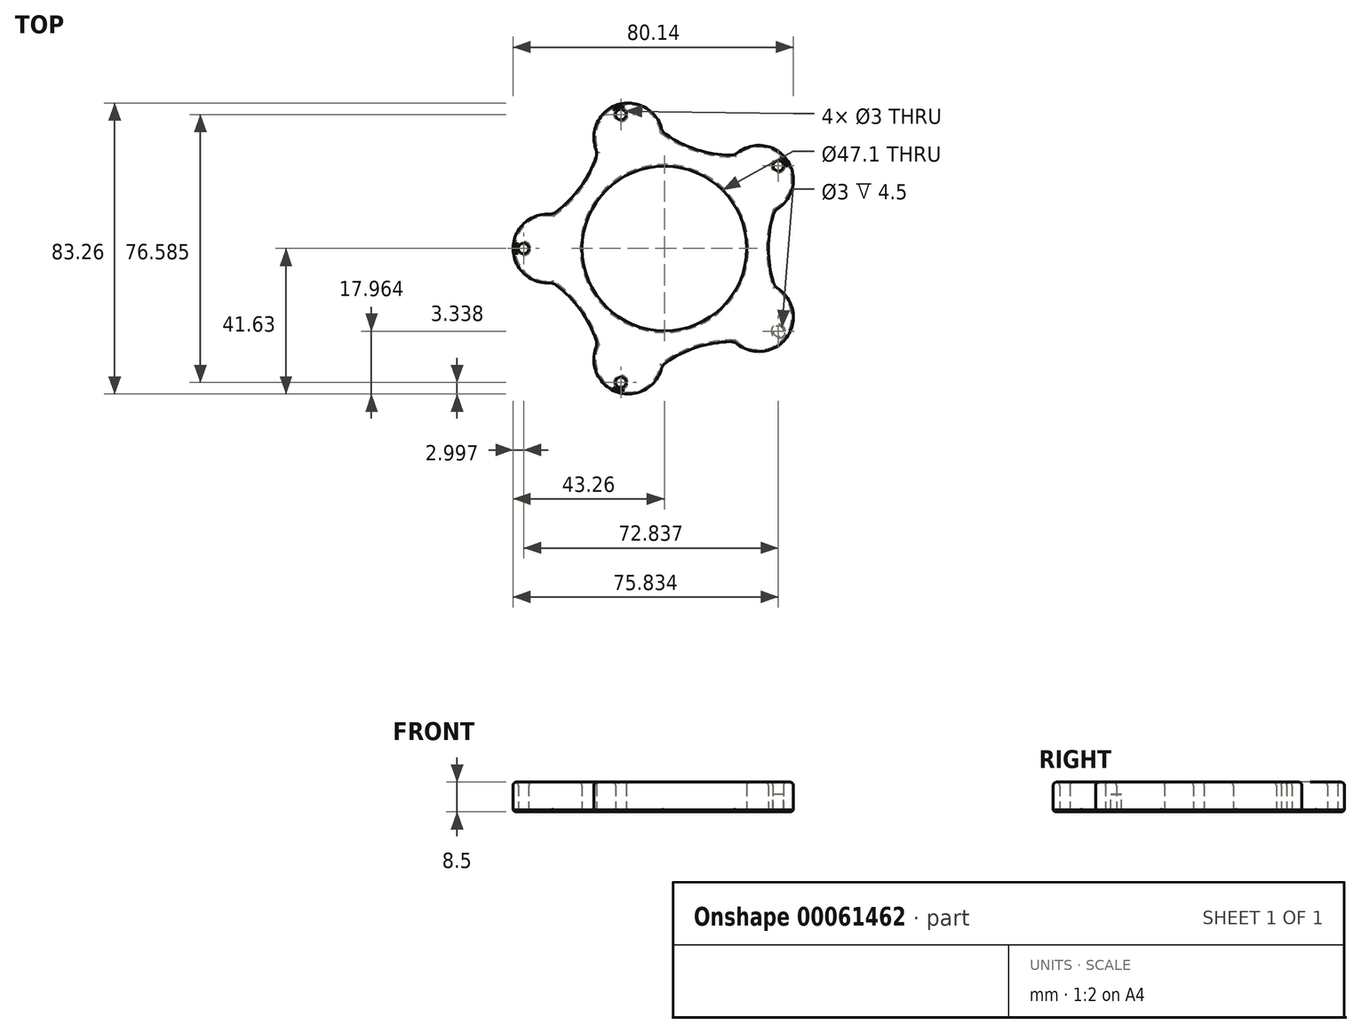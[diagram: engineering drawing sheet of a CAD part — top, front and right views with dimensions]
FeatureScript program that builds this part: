
annotation { "Feature Type Name" : "Feature", "Feature Type Description" : "" }
export const myFeature = defineFeature(function(context is Context, id is Id, definition is map)
    precondition{}
    {
        {
            var Q0;
            Q0=qCreatedBy(makeId("Top.planeOp"),FACE);
            var sketch = newSketch(context, id + "F0", { "sketchPlane" : qUnion([Q0])});
            skCircle(sketch, "E0", {"center": v(32.57, -23.67) * mm, "radius": 1.5 * mm});
            skCircle(sketch, "E1", {"center": v(32.57, 23.67) * mm, "radius": 1.5 * mm});
            skCircle(sketch, "E2", {"center": v(-12.44, 38.3) * mm, "radius": 1.5 * mm});
            skCircle(sketch, "E3", {"center": v(-40.26, 0) * mm, "radius": 1.5 * mm});
            skCircle(sketch, "E4", {"center": v(-12.44, -38.3) * mm, "radius": 1.5 * mm});
            skArc(sketch, "E5", {"start": v(9.2, 28.3) * mm, "mid": v(4.08, 30.44) * mm, "end": v(-0.6, 33.4) * mm});
            skArc(sketch, "E6", {"start": v(-0.6, 33.4) * mm, "mid": v(-5.96, 40.6) * mm, "end": v(-14.93, 40.48) * mm});
            skArc(sketch, "E7", {"start": v(-14.93, 40.48) * mm, "mid": v(-19.7, 34.79) * mm, "end": v(-19.14, 27.38) * mm});
            skArc(sketch, "E8", {"start": v(-19.14, 27.38) * mm, "mid": v(-21.2, 22.23) * mm, "end": v(-24.07, 17.49) * mm});
            skArc(sketch, "E9", {"start": v(-24.07, 17.49) * mm, "mid": v(-27.7, 13.3) * mm, "end": v(-31.95, 9.75) * mm});
            skArc(sketch, "E10", {"start": v(-31.95, 9.75) * mm, "mid": v(-35.07, 9.71) * mm, "end": v(-38.02, 8.71) * mm});
            skArc(sketch, "E11", {"start": v(-38.02, 8.71) * mm, "mid": v(-43.26, 0.36) * mm, "end": v(-38.65, -8.35) * mm});
            skArc(sketch, "E12", {"start": v(-38.65, -8.35) * mm, "mid": v(-35.43, -9.65) * mm, "end": v(-31.95, -9.75) * mm});
            skArc(sketch, "E13", {"start": v(-31.95, -9.75) * mm, "mid": v(-27.7, -13.3) * mm, "end": v(-24.07, -17.49) * mm});
            skArc(sketch, "E14", {"start": v(-24.07, -17.49) * mm, "mid": v(-21.2, -22.23) * mm, "end": v(-19.14, -27.38) * mm});
            skArc(sketch, "E15", {"start": v(-19.14, -27.38) * mm, "mid": v(-19.81, -34.44) * mm, "end": v(-15.56, -40.12) * mm});
            skArc(sketch, "E16", {"start": v(-15.56, -40.12) * mm, "mid": v(-6.29, -40.76) * mm, "end": v(-0.6, -33.4) * mm});
            skArc(sketch, "E17", {"start": v(-0.6, -33.4) * mm, "mid": v(4.08, -30.44) * mm, "end": v(9.2, -28.3) * mm});
            skArc(sketch, "E18", {"start": v(9.2, -28.3) * mm, "mid": v(14.6, -27.03) * mm, "end": v(20.12, -26.67) * mm});
            skArc(sketch, "E19", {"start": v(20.12, -26.67) * mm, "mid": v(20.92, -27.37) * mm, "end": v(21.79, -27.98) * mm});
            skArc(sketch, "E20", {"start": v(21.79, -27.98) * mm, "mid": v(31.64, -28.35) * mm, "end": v(36.88, -20) * mm});
            skArc(sketch, "E21", {"start": v(36.88, -20) * mm, "mid": v(35.55, -14.68) * mm, "end": v(31.58, -10.9) * mm});
            skArc(sketch, "E22", {"start": v(31.58, -10.9) * mm, "mid": v(30.21, -5.52) * mm, "end": v(29.75, 0) * mm});
            skArc(sketch, "E23", {"start": v(29.75, 0) * mm, "mid": v(30.21, 5.52) * mm, "end": v(31.58, 10.9) * mm});
            skArc(sketch, "E24", {"start": v(31.58, 10.9) * mm, "mid": v(35.36, 14.37) * mm, "end": v(36.88, 19.27) * mm});
            skArc(sketch, "E25", {"start": v(36.88, 19.27) * mm, "mid": v(32.27, 27.98) * mm, "end": v(22.42, 28.35) * mm});
            skArc(sketch, "E26", {"start": v(22.42, 28.35) * mm, "mid": v(21.2, 27.6) * mm, "end": v(20.12, 26.67) * mm});
            skArc(sketch, "E27", {"start": v(20.12, 26.67) * mm, "mid": v(14.6, 27.03) * mm, "end": v(9.2, 28.3) * mm});
            skArc(sketch, "E28", {"start": v(21.78, -8.95) * mm, "mid": v(23.1, -4.56) * mm, "end": v(23.55, 0) * mm});
            skArc(sketch, "E29", {"start": v(23.55, 0) * mm, "mid": v(23.1, 4.56) * mm, "end": v(21.78, 8.95) * mm});
            skArc(sketch, "E30", {"start": v(21.78, 8.95) * mm, "mid": v(19.05, 13.84) * mm, "end": v(15.25, 17.95) * mm});
            skArc(sketch, "E31", {"start": v(15.25, 17.95) * mm, "mid": v(7.28, 22.4) * mm, "end": v(-1.79, 23.48) * mm});
            skArc(sketch, "E32", {"start": v(-1.79, 23.48) * mm, "mid": v(-6.95, 22.5) * mm, "end": v(-11.78, 20.4) * mm});
            skArc(sketch, "E33", {"start": v(-11.78, 20.4) * mm, "mid": v(-12.07, 20.22) * mm, "end": v(-12.36, 20.05) * mm});
            skArc(sketch, "E34", {"start": v(-12.36, 20.05) * mm, "mid": v(-19.05, 13.84) * mm, "end": v(-22.89, 5.56) * mm});
            skArc(sketch, "E35", {"start": v(-22.89, 5.56) * mm, "mid": v(-23.55, 0) * mm, "end": v(-22.89, -5.56) * mm});
            skArc(sketch, "E36", {"start": v(-22.89, -5.56) * mm, "mid": v(-19.05, -13.84) * mm, "end": v(-12.36, -20.05) * mm});
            skArc(sketch, "E37", {"start": v(-12.36, -20.05) * mm, "mid": v(-12.07, -20.22) * mm, "end": v(-11.78, -20.4) * mm});
            skArc(sketch, "E38", {"start": v(-11.78, -20.4) * mm, "mid": v(-6.95, -22.5) * mm, "end": v(-1.79, -23.48) * mm});
            skArc(sketch, "E39", {"start": v(-1.79, -23.48) * mm, "mid": v(7.28, -22.4) * mm, "end": v(15.25, -17.95) * mm});
            skArc(sketch, "E40", {"start": v(15.25, -17.95) * mm, "mid": v(19.05, -13.84) * mm, "end": v(21.78, -8.95) * mm});
            skCircle(sketch, "E41", {"center": v(0, 0) * mm, "radius": 43.26 * mm});
            skSolve(sketch);
        }
        {
            var Q0;
            Q0=makeQuery(id+"F0.imprint","IMPRINT",FACE,{"disambiguationData":[TD([[makeQuery(id+"F0.imprint","IMPRINT",EDGE,{"derivedFrom":sQuery(id+"F0.wireOp",EDGE,"E0")}),1.0]])]});
            var Q1;
            Q1=makeQuery(id+"F0.imprint","IMPRINT",FACE,{"disambiguationData":[TD([[makeQuery(id+"F0.imprint","IMPRINT",EDGE,{"derivedFrom":sQuery(id+"F0.wireOp",EDGE,"E1")}),-1.0]])]});
            var Q2;
            Q2=makeQuery(id+"F0.imprint","IMPRINT",FACE,{"disambiguationData":[TD([[makeQuery(id+"F0.imprint","IMPRINT",EDGE,{"derivedFrom":sQuery(id+"F0.wireOp",EDGE,"E2")}),-1.0]])]});
            var Q3;
            Q3=makeQuery(id+"F0.imprint","IMPRINT",FACE,{"disambiguationData":[TD([[makeQuery(id+"F0.imprint","IMPRINT",EDGE,{"derivedFrom":sQuery(id+"F0.wireOp",EDGE,"E3")}),-1.0]])]});
            var Q4;
            Q4=makeQuery(id+"F0.imprint","IMPRINT",FACE,{"disambiguationData":[TD([[makeQuery(id+"F0.imprint","IMPRINT",EDGE,{"derivedFrom":sQuery(id+"F0.wireOp",EDGE,"E4")}),-1.0]])]});
            var Q5;
            Q5=makeQuery(id+"F0.imprint","IMPRINT",FACE,{"disambiguationData":[TD([[makeQuery(id+"F0.imprint","IMPRINT",EDGE,{"derivedFrom":sQuery(id+"F0.wireOp",EDGE,"E0")}),-1.0]])]});
            extrude(context, id + "F1", {"entities" : qUnion([Q0, Q1, Q2, Q3, Q4, Q5]), "depth" : 3.5 * mm});
        }
        {
            var Q0;
            Q0=makeQuery(id+"F0.imprint","IMPRINT",FACE,{"disambiguationData":[TD([[makeQuery(id+"F0.imprint","IMPRINT",EDGE,{"derivedFrom":sQuery(id+"F0.wireOp",EDGE,"E2")}),-1.0]])]});
            var Q1;
            Q1=makeQuery(id+"F0.imprint","IMPRINT",FACE,{"disambiguationData":[TD([[makeQuery(id+"F0.imprint","IMPRINT",EDGE,{"derivedFrom":sQuery(id+"F0.wireOp",EDGE,"E3")}),-1.0]])]});
            var Q2;
            Q2=makeQuery(id+"F0.imprint","IMPRINT",FACE,{"disambiguationData":[TD([[makeQuery(id+"F0.imprint","IMPRINT",EDGE,{"derivedFrom":sQuery(id+"F0.wireOp",EDGE,"E1")}),-1.0]])]});
            var Q3;
            Q3=makeQuery(id+"F0.imprint","IMPRINT",FACE,{"disambiguationData":[TD([[makeQuery(id+"F0.imprint","IMPRINT",EDGE,{"derivedFrom":sQuery(id+"F0.wireOp",EDGE,"E0")}),-1.0]])]});
            var Q4;
            Q4=makeQuery(id+"F0.imprint","IMPRINT",FACE,{"disambiguationData":[TD([[makeQuery(id+"F0.imprint","IMPRINT",EDGE,{"derivedFrom":sQuery(id+"F0.wireOp",EDGE,"E4")}),-1.0]])]});
            extrude(context, id + "F2", {"entities" : qUnion([Q0, Q1, Q2, Q3, Q4]), "operationType" : NewBodyOperationType.ADD, "oppositeDirection" : true, "depth" : 5 * mm});
        }
        {
            var Q0;
            Q0=makeQuery(id+"F2.opExtrude","CAP_FACE",FACE,{"disambiguationData":[OSD([sQuery(id+"F0.wireOp",EDGE,"E0")])],"isStart":false});
            var Q1;
            Q1=makeQuery(id+"F2.opExtrude","CAP_FACE",FACE,{"disambiguationData":[OSD([sQuery(id+"F0.wireOp",EDGE,"E1")])],"isStart":false});
            var Q2;
            Q2=makeQuery(id+"F2.opExtrude","CAP_FACE",FACE,{"disambiguationData":[OSD([sQuery(id+"F0.wireOp",EDGE,"E2")])],"isStart":false});
            var Q3;
            Q3=makeQuery(id+"F2.opExtrude","CAP_FACE",FACE,{"disambiguationData":[OSD([sQuery(id+"F0.wireOp",EDGE,"E3")])],"isStart":false});
            var Q4;
            Q4=makeQuery(id+"F2.opExtrude","CAP_FACE",FACE,{"disambiguationData":[OSD([sQuery(id+"F0.wireOp",EDGE,"E4")])],"isStart":false});
            chamfer(context, id + "F3", {"entities" : qUnion([Q0, Q1, Q2, Q3, Q4]), "width" : .5 * mm, "tangentPropagation" : true});
        }
        {
            var Q0;
            Q0=makeQuery(id+"F1.opExtrude","SWEPT_EDGE",EDGE,{"disambiguationData":[OSD([sQuery(id+"F0.wireOp",EDGE,"E12"),sQuery(id+"F0.wireOp",EDGE,"E13")])]});
            var Q1;
            Q1=makeQuery(id+"F1.opExtrude","SWEPT_EDGE",EDGE,{"disambiguationData":[OSD([sQuery(id+"F0.wireOp",EDGE,"E16"),sQuery(id+"F0.wireOp",EDGE,"E17")])]});
            var Q2;
            Q2=makeQuery(id+"F1.opExtrude","SWEPT_EDGE",EDGE,{"disambiguationData":[OSD([sQuery(id+"F0.wireOp",EDGE,"E18"),sQuery(id+"F0.wireOp",EDGE,"E19")])]});
            var Q3;
            Q3=makeQuery(id+"F1.opExtrude","SWEPT_EDGE",EDGE,{"disambiguationData":[OSD([sQuery(id+"F0.wireOp",EDGE,"E14"),sQuery(id+"F0.wireOp",EDGE,"E15")])]});
            var Q4;
            Q4=makeQuery(id+"F1.opExtrude","SWEPT_EDGE",EDGE,{"disambiguationData":[OSD([sQuery(id+"F0.wireOp",EDGE,"E9"),sQuery(id+"F0.wireOp",EDGE,"E10")])]});
            var Q5;
            Q5=makeQuery(id+"F1.opExtrude","SWEPT_EDGE",EDGE,{"disambiguationData":[OSD([sQuery(id+"F0.wireOp",EDGE,"E7"),sQuery(id+"F0.wireOp",EDGE,"E8")])]});
            var Q6;
            Q6=makeQuery(id+"F1.opExtrude","SWEPT_EDGE",EDGE,{"disambiguationData":[OSD([sQuery(id+"F0.wireOp",EDGE,"E5"),sQuery(id+"F0.wireOp",EDGE,"E6")])]});
            var Q7;
            Q7=makeQuery(id+"F1.opExtrude","SWEPT_EDGE",EDGE,{"disambiguationData":[OSD([sQuery(id+"F0.wireOp",EDGE,"E26"),sQuery(id+"F0.wireOp",EDGE,"E27")])]});
            var Q8;
            Q8=makeQuery(id+"F1.opExtrude","SWEPT_EDGE",EDGE,{"disambiguationData":[OSD([sQuery(id+"F0.wireOp",EDGE,"E23"),sQuery(id+"F0.wireOp",EDGE,"E24")])]});
            var Q9;
            Q9=makeQuery(id+"F1.opExtrude","SWEPT_EDGE",EDGE,{"disambiguationData":[OSD([sQuery(id+"F0.wireOp",EDGE,"E21"),sQuery(id+"F0.wireOp",EDGE,"E22")])]});
            fillet(context, id + "F4", {"entities" : qUnion([Q0, Q1, Q2, Q3, Q4, Q5, Q6, Q7, Q8, Q9]), "radius" : 3 * mm, "tangentPropagation" : true, "allowEdgeOverflow" : false});
        }
        {
            var Q0;
            Q0=makeQuery(id+"F1.opExtrude","CAP_FACE",FACE,{"disambiguationData":[OSD([sQuery(id+"F0.wireOp",EDGE,"E5"),sQuery(id+"F0.wireOp",EDGE,"E6"),sQuery(id+"F0.wireOp",EDGE,"E7"),sQuery(id+"F0.wireOp",EDGE,"E8"),sQuery(id+"F0.wireOp",EDGE,"E9"),sQuery(id+"F0.wireOp",EDGE,"E10"),sQuery(id+"F0.wireOp",EDGE,"E11"),sQuery(id+"F0.wireOp",EDGE,"E12"),sQuery(id+"F0.wireOp",EDGE,"E13"),sQuery(id+"F0.wireOp",EDGE,"E14"),sQuery(id+"F0.wireOp",EDGE,"E15"),sQuery(id+"F0.wireOp",EDGE,"E16"),sQuery(id+"F0.wireOp",EDGE,"E17"),sQuery(id+"F0.wireOp",EDGE,"E18"),sQuery(id+"F0.wireOp",EDGE,"E19"),sQuery(id+"F0.wireOp",EDGE,"E20"),sQuery(id+"F0.wireOp",EDGE,"E21"),sQuery(id+"F0.wireOp",EDGE,"E22"),sQuery(id+"F0.wireOp",EDGE,"E23"),sQuery(id+"F0.wireOp",EDGE,"E24"),sQuery(id+"F0.wireOp",EDGE,"E25"),sQuery(id+"F0.wireOp",EDGE,"E26"),sQuery(id+"F0.wireOp",EDGE,"E27"),sQuery(id+"F0.wireOp",EDGE,"E28"),sQuery(id+"F0.wireOp",EDGE,"E29"),sQuery(id+"F0.wireOp",EDGE,"E30"),sQuery(id+"F0.wireOp",EDGE,"E31"),sQuery(id+"F0.wireOp",EDGE,"E32"),sQuery(id+"F0.wireOp",EDGE,"E33"),sQuery(id+"F0.wireOp",EDGE,"E34"),sQuery(id+"F0.wireOp",EDGE,"E35"),sQuery(id+"F0.wireOp",EDGE,"E36"),sQuery(id+"F0.wireOp",EDGE,"E37"),sQuery(id+"F0.wireOp",EDGE,"E38"),sQuery(id+"F0.wireOp",EDGE,"E39"),sQuery(id+"F0.wireOp",EDGE,"E40")])],"isStart":false});
            fillet(context, id + "F5", {"entities" : qUnion([Q0]), "radius" : 1 * mm, "tangentPropagation" : true, "allowEdgeOverflow" : false});
        }
    });
